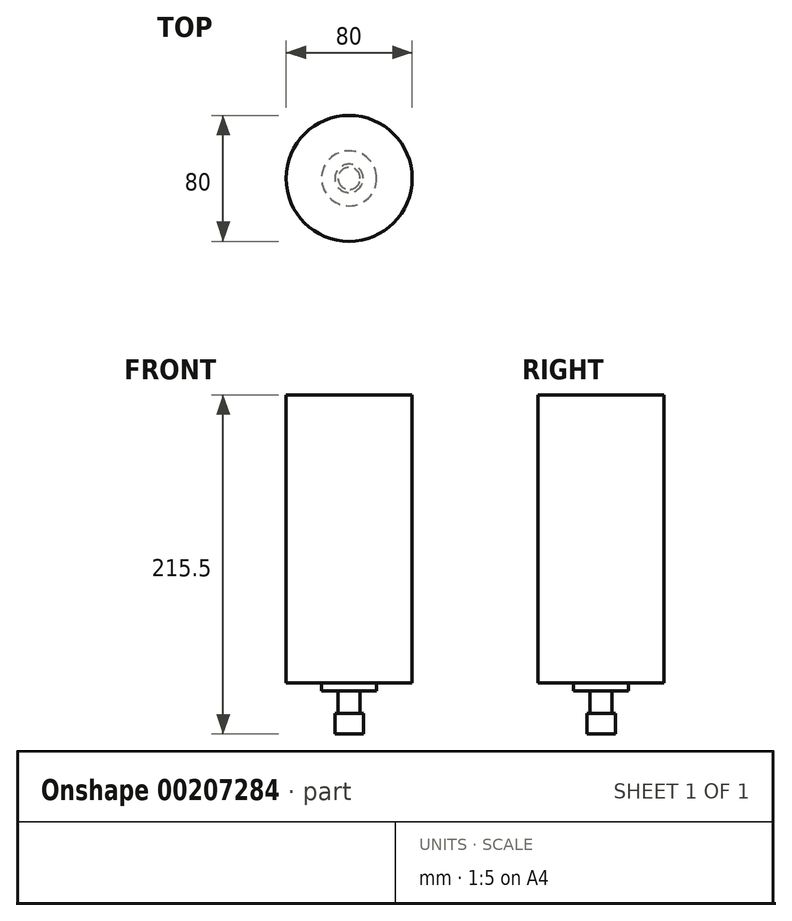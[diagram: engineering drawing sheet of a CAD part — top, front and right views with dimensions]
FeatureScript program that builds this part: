
annotation { "Feature Type Name" : "Feature", "Feature Type Description" : "" }
export const myFeature = defineFeature(function(context is Context, id is Id, definition is map)
    precondition{}
    {
        {
            var Q0;
            Q0=qCreatedBy(makeId("Front.planeOp"),FACE);
            var sketch = newSketch(context, id + "F0", { "sketchPlane" : qUnion([Q0])});
            skLineSegment(sketch, "E0", {"start": v(0, 0) * mm, "end": v(0, 215.5) * mm, "construction": true});
            skLineSegment(sketch, "E1", {"start": v(0, 215.5) * mm, "end": v(40, 215.5) * mm});
            skLineSegment(sketch, "E2", {"start": v(40, 215.5) * mm, "end": v(40, 32.5) * mm});
            skLineSegment(sketch, "E3", {"start": v(40, 32.5) * mm, "end": v(17.5, 32.5) * mm});
            skLineSegment(sketch, "E4", {"start": v(17.5, 32.5) * mm, "end": v(17.5, 27.5) * mm});
            skLineSegment(sketch, "E5", {"start": v(17.5, 27.5) * mm, "end": v(7, 27.5) * mm});
            skLineSegment(sketch, "E6", {"start": v(7, 27.5) * mm, "end": v(7, 0) * mm});
            skLineSegment(sketch, "E7", {"start": v(7, 0) * mm, "end": v(0, 0) * mm});
            skLineSegment(sketch, "E8", {"start": v(0, 215.5) * mm, "end": v(0, 0) * mm});
            skSolve(sketch);
        }
        {
            var Q0;
            Q0 = qSketchRegion(id + "F0", true);
            var Q1;
            Q1=sQuery(id+"F0.wireOp",EDGE,"E8");
            revolve(context, id + "F1", {"entities" : qUnion([Q0]), "axis" : qUnion([Q1]), "revolveType" : RevolveType.FULL});
        }
        {
            var Q0;
            Q0=makeQuery(id+"F1.opRevolve","SWEPT_FACE",FACE,{"disambiguationData":[OSD([sQuery(id+"F0.wireOp",EDGE,"E7")])]});
            var sketch = newSketch(context, id + "F2", { "sketchPlane" : qUnion([Q0])});
            skCircle(sketch, "E9", {"center": v(0, 0) * mm, "radius": 9 * mm});
            skSolve(sketch);
        }
        {
            var Q0;
            Q0 = qSketchRegion(id + "F2", true);
            extrude(context, id + "F3", {"entities" : qUnion([Q0]), "operationType" : NewBodyOperationType.ADD, "oppositeDirection" : true, "depth" : 13 * mm});
        }
    });
